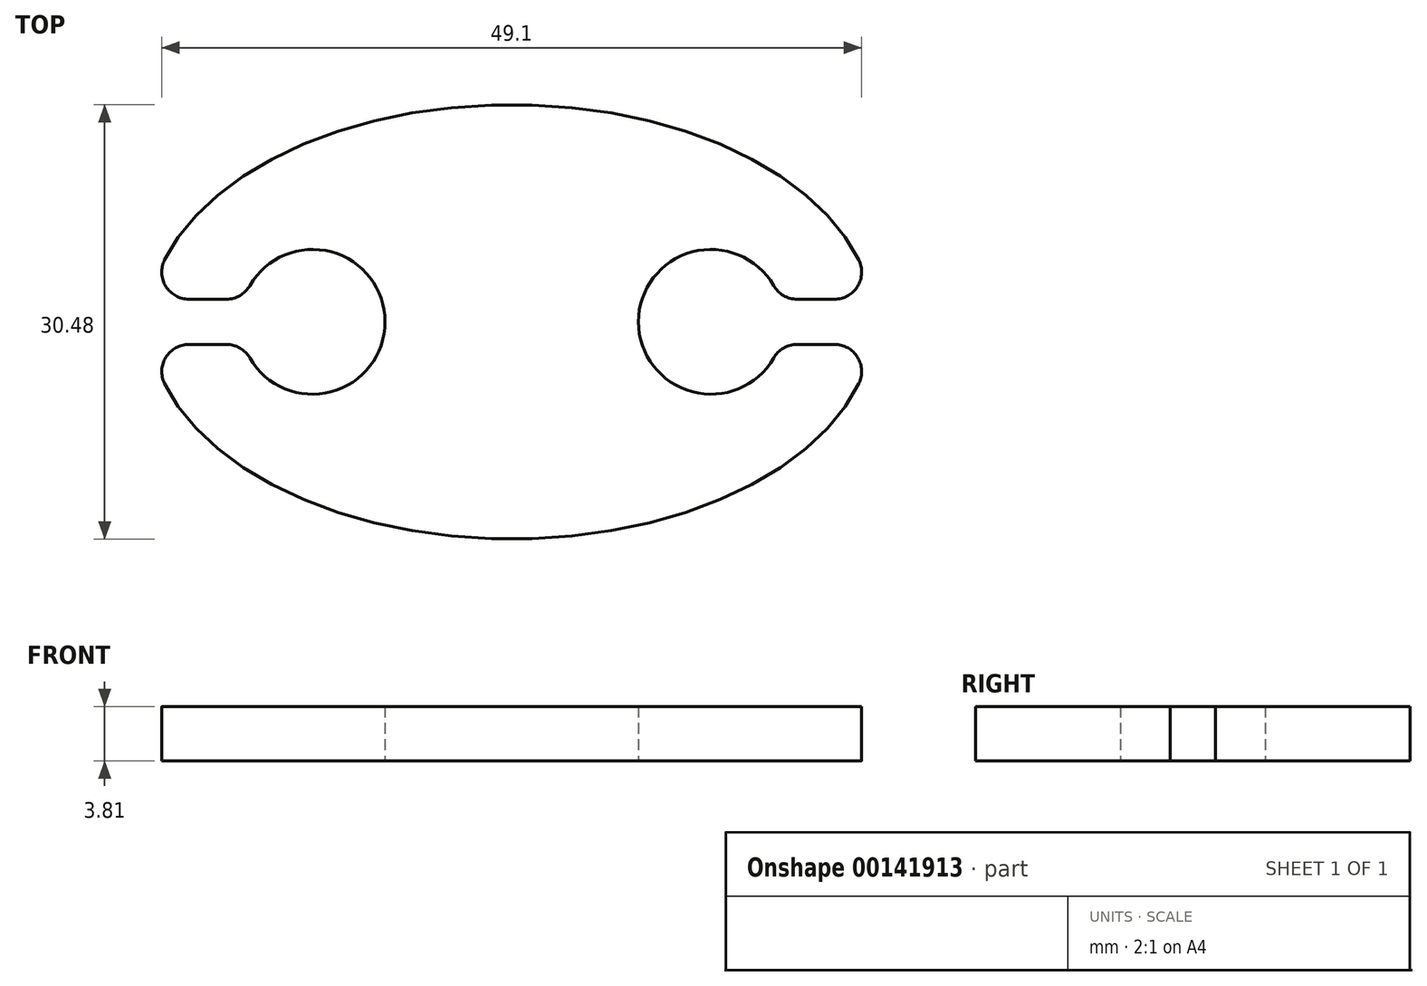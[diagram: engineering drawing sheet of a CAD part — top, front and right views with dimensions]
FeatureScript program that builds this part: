
annotation { "Feature Type Name" : "Feature", "Feature Type Description" : "" }
export const myFeature = defineFeature(function(context is Context, id is Id, definition is map)
    precondition{}
    {
        {
            var Q0;
            Q0=qCreatedBy(makeId("Top.planeOp"),FACE);
            var sketch = newSketch(context, id + "F0", { "sketchPlane" : qUnion([Q0])});
            skEllipse(sketch, "E0", {"center": v(0, 0) * mm, "majorRadius": 25.4 * mm, "minorRadius": 15.24 * mm, "majorAxis": v(-1, 0)});
            skPoint(sketch, "E1.startSnap0", {"position": v(-25.4, 0) * mm});
            skLineSegment(sketch, "E2", {"start": v(-25.4, 0) * mm, "end": v(25.4, 0) * mm});
            skSolve(sketch);
        }
        {
            var Q0;
            Q0 = qSketchRegion(id + "F0", true);
            extrude(context, id + "F1", {"entities" : qUnion([Q0]), "depth" : 3.8 * mm});
        }
        {
            var Q0;
            Q0=qCreatedBy(makeId("Top.planeOp"),FACE);
            var sketch = newSketch(context, id + "F2", { "sketchPlane" : qUnion([Q0])});
            skCircle(sketch, "E3", {"center": v(13.97, 0) * mm, "radius": 5.08 * mm});
            skCircle(sketch, "E4", {"center": v(-13.97, 0) * mm, "radius": 5.08 * mm});
            skLineSegment(sketch, "E5", {"start": v(-18.8, 1.59) * mm, "end": v(-24.93, 1.59) * mm});
            skLineSegment(sketch, "E6", {"start": v(-18.8, -1.59) * mm, "end": v(-24.93, -1.59) * mm});
            skLineSegment(sketch, "E7", {"start": v(18.8, 1.59) * mm, "end": v(25.74, 1.59) * mm});
            skLineSegment(sketch, "E8", {"start": v(18.8, -1.59) * mm, "end": v(25.26, -1.59) * mm});
            skArc(sketch, "E9", {"start": v(-24.93, 1.59) * mm, "mid": v(-26.52, 0) * mm, "end": v(-24.93, -1.59) * mm});
            skArc(sketch, "E10", {"start": v(25.74, 1.59) * mm, "mid": v(27.35, -0.28) * mm, "end": v(25.26, -1.59) * mm});
            skSolve(sketch);
        }
        {
            var Q0;
            Q0 = qSketchRegion(id + "F2", true);
            extrude(context, id + "F3", {"entities" : qUnion([Q0]), "operationType" : NewBodyOperationType.REMOVE, "endBound" : BoundingType.THROUGH_ALL, "depth" : 25.4 * mm});
        }
        {
            var Q0;
            Q0=makeQuery(id+"F3.boolean.opBoolean","INTERSECT",EDGE,{"derivedFrom":[makeQuery(id+"F1.opExtrude","SWEPT_FACE",FACE,{"disambiguationData":[OSD([sQuery(id+"F0.wireOp",EDGE,"E0")])]}),makeQuery(id+"F3.opExtrude","SWEPT_FACE",FACE,{"disambiguationData":[OSD([sQuery(id+"F2.wireOp",EDGE,"E7")])]})]});
            var Q1;
            Q1=makeQuery(id+"F3.boolean.opBoolean","COPY",EDGE,{"derivedFrom":makeQuery(id+"F3.opExtrude","SWEPT_EDGE",EDGE,{"disambiguationData":[OSD([sQuery(id+"F2.wireOp",EDGE,"E4"),sQuery(id+"F2.wireOp",EDGE,"E6")])]})});
            var Q2;
            Q2=makeQuery(id+"F3.boolean.opBoolean","INTERSECT",EDGE,{"disambiguationData":[OD(1.0)],"derivedFrom":[makeQuery(id+"F1.opExtrude","SWEPT_FACE",FACE,{"disambiguationData":[OSD([sQuery(id+"F0.wireOp",EDGE,"E0")])]}),makeQuery(id+"F3.opExtrude","SWEPT_FACE",FACE,{"disambiguationData":[OSD([sQuery(id+"F2.wireOp",EDGE,"E9")])]})]});
            var Q3;
            Q3=makeQuery(id+"F3.boolean.opBoolean","INTERSECT",EDGE,{"disambiguationData":[OD(0.0)],"derivedFrom":[makeQuery(id+"F1.opExtrude","SWEPT_FACE",FACE,{"disambiguationData":[OSD([sQuery(id+"F0.wireOp",EDGE,"E0")])]}),makeQuery(id+"F3.opExtrude","SWEPT_FACE",FACE,{"disambiguationData":[OSD([sQuery(id+"F2.wireOp",EDGE,"E9")])]})]});
            var Q4;
            Q4=makeQuery(id+"F3.boolean.opBoolean","COPY",EDGE,{"derivedFrom":makeQuery(id+"F3.opExtrude","SWEPT_EDGE",EDGE,{"disambiguationData":[OSD([sQuery(id+"F2.wireOp",EDGE,"E3"),sQuery(id+"F2.wireOp",EDGE,"E7")])]})});
            var Q5;
            Q5=makeQuery(id+"F3.boolean.opBoolean","COPY",EDGE,{"derivedFrom":makeQuery(id+"F3.opExtrude","SWEPT_EDGE",EDGE,{"disambiguationData":[OSD([sQuery(id+"F2.wireOp",EDGE,"E4"),sQuery(id+"F2.wireOp",EDGE,"E5")])]})});
            fillet(context, id + "F4", {"entities" : qUnion([Q0, Q1, Q2, Q3, Q4, Q5]), "radius" : 1.9 * mm, "tangentPropagation" : true, "allowEdgeOverflow" : false});
        }
        {
            var Q0;
            Q0=makeQuery(id+"F3.boolean.opBoolean","COPY",EDGE,{"derivedFrom":makeQuery(id+"F3.opExtrude","SWEPT_EDGE",EDGE,{"disambiguationData":[OSD([sQuery(id+"F2.wireOp",EDGE,"E8"),sQuery(id+"F2.wireOp",EDGE,"E10")])]})});
            var Q1;
            Q1=makeQuery(id+"F3.boolean.opBoolean","COPY",EDGE,{"derivedFrom":makeQuery(id+"F3.opExtrude","SWEPT_EDGE",EDGE,{"disambiguationData":[OSD([sQuery(id+"F2.wireOp",EDGE,"E3"),sQuery(id+"F2.wireOp",EDGE,"E8")])]})});
            fillet(context, id + "F5", {"entities" : qUnion([Q0, Q1]), "radius" : 1.9 * mm, "tangentPropagation" : true, "allowEdgeOverflow" : false});
        }
    });
